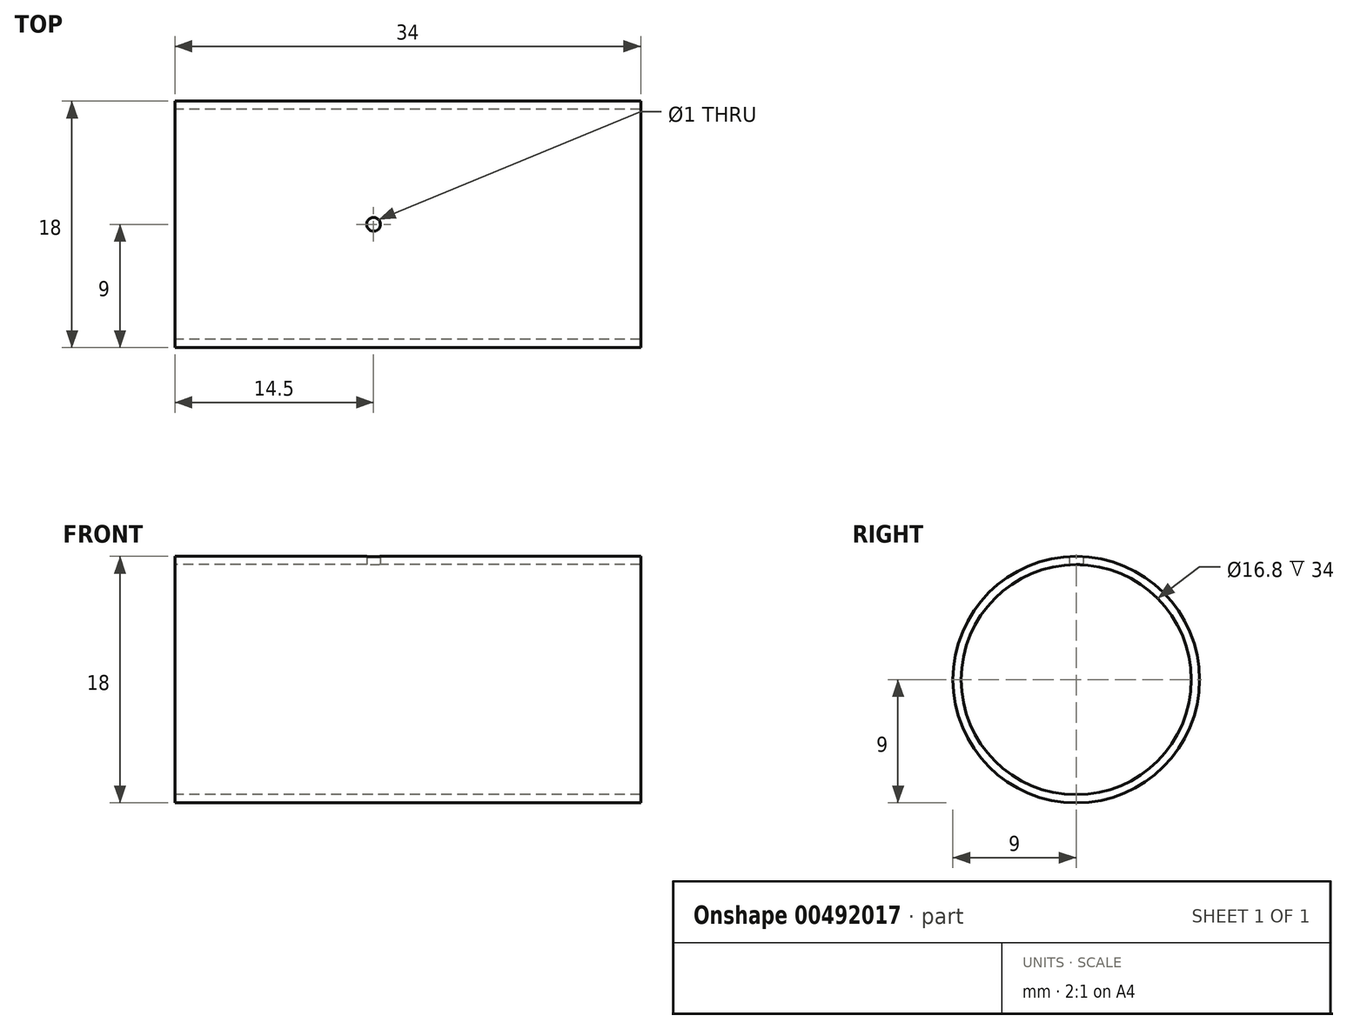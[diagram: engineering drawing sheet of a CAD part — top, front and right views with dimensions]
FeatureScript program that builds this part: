
annotation { "Feature Type Name" : "Feature", "Feature Type Description" : "" }
export const myFeature = defineFeature(function(context is Context, id is Id, definition is map)
    precondition{}
    {
        {
            var Q0;
            Q0=qCreatedBy(makeId("Right.planeOp"),FACE);
            var sketch = newSketch(context, id + "F0", { "sketchPlane" : qUnion([Q0])});
            skCircle(sketch, "E0", {"center": v(0, 0) * mm, "radius": 9 * mm});
            skCircle(sketch, "E1", {"center": v(0, 0) * mm, "radius": 8.4 * mm});
            skSolve(sketch);
        }
        {
            var Q0;
            Q0 = qSketchRegion(id + "F0", true);
            extrude(context, id + "F1", {"entities" : qUnion([Q0]), "depth" : 34 * mm});
        }
        {
            var Q0;
            Q0=qCreatedBy(makeId("Front.planeOp"),FACE);
            var sketch = newSketch(context, id + "F2", { "sketchPlane" : qUnion([Q0])});
            skLineSegment(sketch, "E2.top", {"start": v(14.5, 6) * mm, "end": v(14, 6) * mm});
            skLineSegment(sketch, "E2.right", {"start": v(14, 9) * mm, "end": v(14, 6) * mm});
            skPoint(sketch, "E2.middle", {"position": v(14.5, 9) * mm});
            skLineSegment(sketch, "E3", {"start": v(14.5, 9) * mm, "end": v(14.5, 6) * mm});
            skPoint(sketch, "E3.endSnap0", {"position": v(14.5, 6) * mm});
            skLineSegment(sketch, "E4", {"start": v(14.5, 9) * mm, "end": v(14, 9) * mm});
            skSolve(sketch);
        }
        {
            var Q0;
            Q0 = qSketchRegion(id + "F2", true);
            var Q1;
            Q1=sQuery(id+"F2.wireOp",EDGE,"E3");
            revolve(context, id + "F3", {"operationType" : NewBodyOperationType.REMOVE, "entities" : qUnion([Q0]), "axis" : qUnion([Q1]), "revolveType" : RevolveType.FULL, "oppositeDirection" : true});
        }
    });
